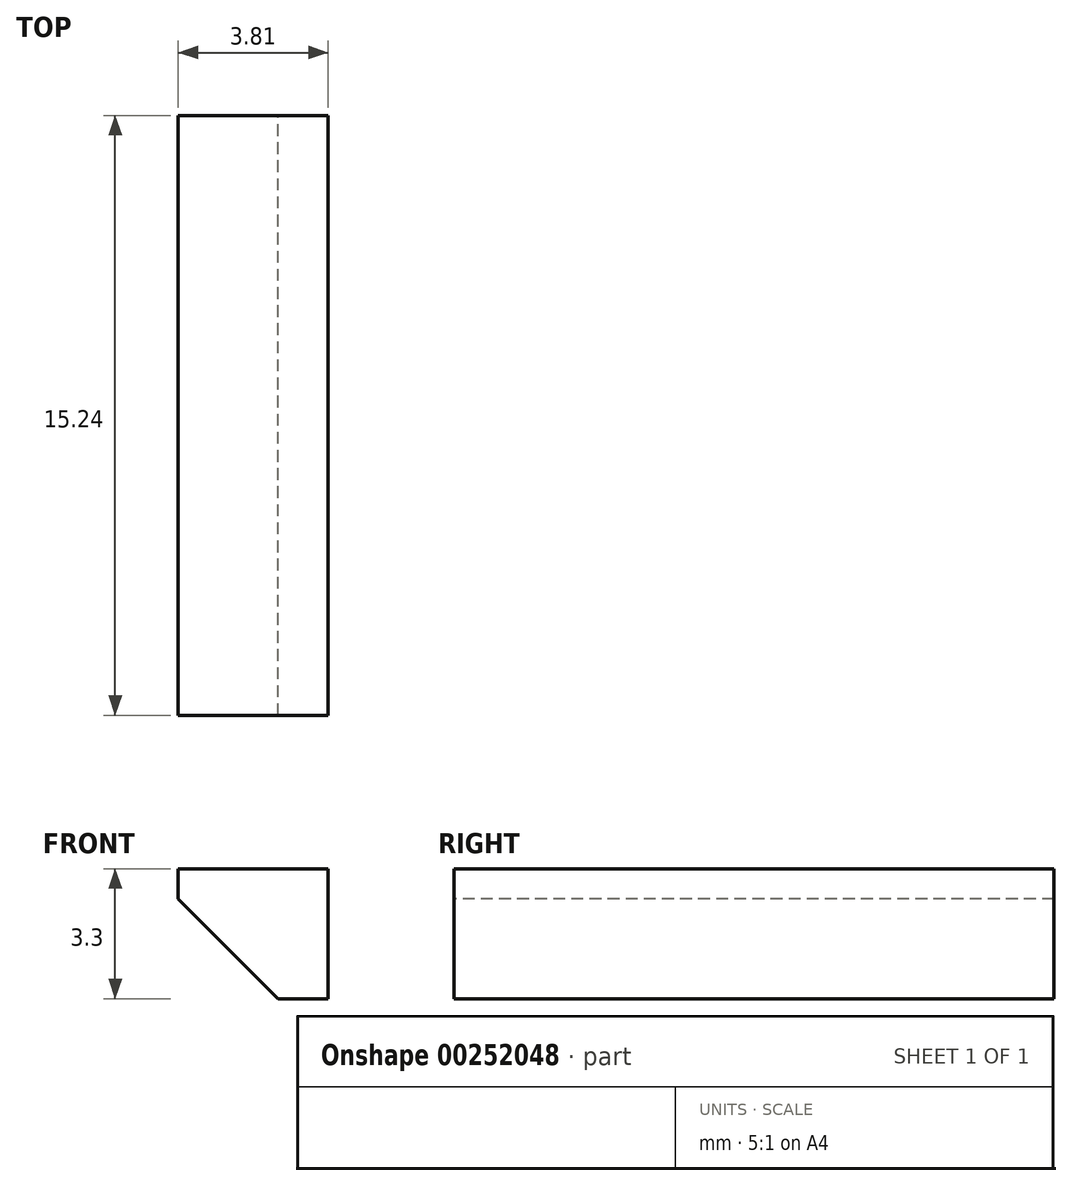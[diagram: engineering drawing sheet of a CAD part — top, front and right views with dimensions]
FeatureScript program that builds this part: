
annotation { "Feature Type Name" : "Feature", "Feature Type Description" : "" }
export const myFeature = defineFeature(function(context is Context, id is Id, definition is map)
    precondition{}
    {
        {
            var Q0;
            Q0=qCreatedBy(makeId("Right.planeOp"),FACE);
            var sketch = newSketch(context, id + "F0", { "sketchPlane" : qUnion([Q0])});
            skLineSegment(sketch, "E0.bottom", {"start": v(7.62, 1.65) * mm, "end": v(-7.62, 1.65) * mm});
            skLineSegment(sketch, "E0.top", {"start": v(7.62, -1.65) * mm, "end": v(-7.62, -1.65) * mm});
            skLineSegment(sketch, "E0.left", {"start": v(7.62, 1.65) * mm, "end": v(7.62, -1.65) * mm});
            skLineSegment(sketch, "E0.right", {"start": v(-7.62, 1.65) * mm, "end": v(-7.62, -1.65) * mm});
            skPoint(sketch, "E0.middle", {"position": v(0, 0) * mm});
            skSolve(sketch);
        }
        {
            var Q0;
            Q0 = qSketchRegion(id + "F0", true);
            extrude(context, id + "F1", {"entities" : qUnion([Q0]), "depth" : 3.8 * mm});
        }
        {
            var Q0;
            Q0=makeQuery(id+"F1.opExtrude","CAP_EDGE",EDGE,{"disambiguationData":[OSD([sQuery(id+"F0.wireOp",EDGE,"E0.top")])],"isStart":true});
            chamfer(context, id + "F2", {"entities" : qUnion([Q0]), "width" : 2.54 * mm, "tangentPropagation" : true});
        }
    });
